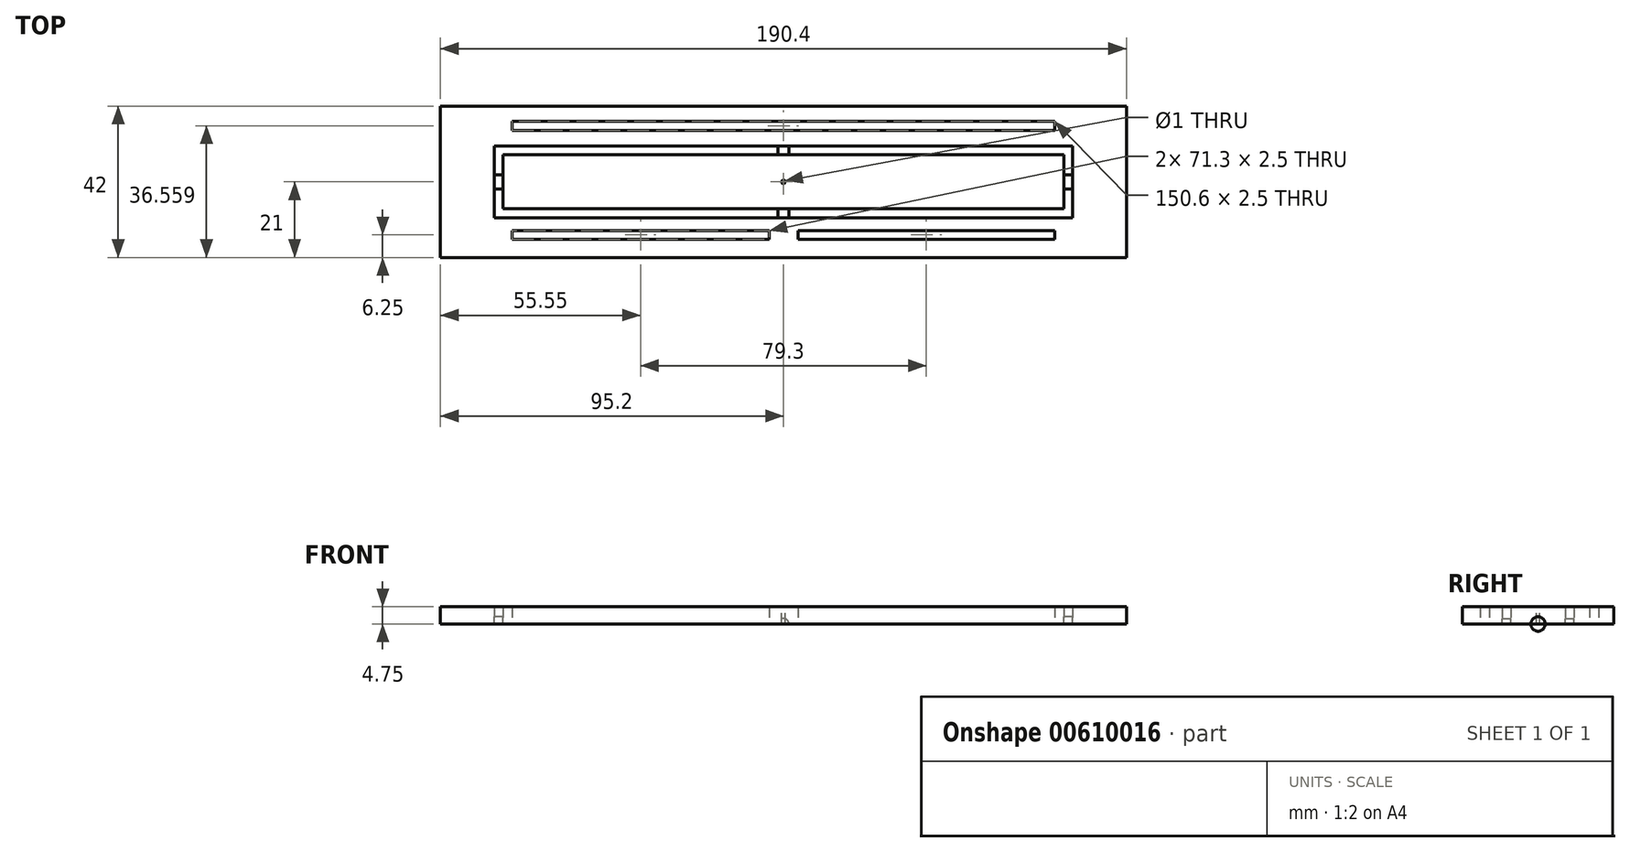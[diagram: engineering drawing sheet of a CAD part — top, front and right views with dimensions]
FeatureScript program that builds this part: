
annotation { "Feature Type Name" : "Feature", "Feature Type Description" : "" }
export const myFeature = defineFeature(function(context is Context, id is Id, definition is map)
    precondition{}
    {
        {
            var Q0;
            Q0=qCreatedBy(makeId("Front.planeOp"),FACE);
            var sketch = newSketch(context, id + "F0", { "sketchPlane" : qUnion([Q0])});
            skPoint(sketch, "E0.middle", {"position": v(0.08, 0) * mm});
            skLineSegment(sketch, "E1", {"start": v(-79.3, 0) * mm, "end": v(79.3, 0) * mm});
            skLineSegment(sketch, "E2.bottom", {"start": v(-79.3, 0) * mm, "end": v(-95.2, 0) * mm});
            skLineSegment(sketch, "E2.right", {"start": v(-95.2, 0) * mm, "end": v(-95.2, 4.75) * mm});
            skLineSegment(sketch, "E3", {"start": v(-79.3, 1) * mm, "end": v(-95.2, 4.75) * mm});
            skLineSegment(sketch, "E4.bottom", {"start": v(79.3, 0) * mm, "end": v(95.2, 0) * mm});
            skArc(sketch, "E5", {"start": v(1.5, 0) * mm, "mid": v(0, 1.5) * mm, "end": v(-1.5, 0) * mm});
            skLineSegment(sketch, "E6", {"start": v(-1.5, 0) * mm, "end": v(1.5, 0) * mm});
            skLineSegment(sketch, "E7", {"start": v(0, 0) * mm, "end": v(0, 4.75) * mm});
            skLineSegment(sketch, "E8", {"start": v(-95.2, 4.75) * mm, "end": v(95.2, 4.75) * mm});
            skLineSegment(sketch, "E9", {"start": v(95.2, 4.75) * mm, "end": v(95.2, 0) * mm});
            skLineSegment(sketch, "E10", {"start": v(79.3, 1) * mm, "end": v(95.2, 4.75) * mm});
            skArc(sketch, "E11", {"start": v(79.3, 1) * mm, "mid": v(0, 4.75) * mm, "end": v(-79.3, 1) * mm});
            skSolve(sketch);
        }
        {
            var Q0;
            Q0=qCreatedBy(makeId("Top.planeOp"),FACE);
            var sketch = newSketch(context, id + "F1", { "sketchPlane" : qUnion([Q0])});
            skPoint(sketch, "E12.middle", {"position": v(0, 0) * mm});
            skLineSegment(sketch, "E13.right", {"start": v(75.3, 16.8) * mm, "end": v(75.3, 14.3) * mm});
            skLineSegment(sketch, "E14.right", {"start": v(75.3, -13.5) * mm, "end": v(75.3, -16) * mm});
            skLineSegment(sketch, "E15.right", {"start": v(4, -13.5) * mm, "end": v(4, -16) * mm});
            skLineSegment(sketch, "E16.right", {"start": v(-4, -13.5) * mm, "end": v(-4, -16) * mm});
            skLineSegment(sketch, "E17.right", {"start": v(-75.3, -13.5) * mm, "end": v(-75.3, -16) * mm});
            skLineSegment(sketch, "E18.right", {"start": v(-75.3, 16.8) * mm, "end": v(-75.3, 14.3) * mm});
            skLineSegment(sketch, "E19", {"start": v(4, -13.5) * mm, "end": v(75.3, -13.5) * mm});
            skLineSegment(sketch, "E20", {"start": v(75.3, -16) * mm, "end": v(4, -16) * mm});
            skLineSegment(sketch, "E21", {"start": v(-75.3, -16) * mm, "end": v(-4, -16) * mm});
            skLineSegment(sketch, "E22", {"start": v(-4, -13.5) * mm, "end": v(-75.3, -13.5) * mm});
            skLineSegment(sketch, "E23", {"start": v(-75.3, 14.3) * mm, "end": v(75.3, 14.3) * mm});
            skLineSegment(sketch, "E24", {"start": v(75.3, 16.8) * mm, "end": v(-75.3, 16.8) * mm});
            skLineSegment(sketch, "E25.bottom", {"start": v(-80.3, 10) * mm, "end": v(80.3, 10) * mm});
            skLineSegment(sketch, "E25.top", {"start": v(-80.3, -10) * mm, "end": v(80.3, -10) * mm});
            skLineSegment(sketch, "E25.left", {"start": v(-80.3, 10) * mm, "end": v(-80.3, -10) * mm});
            skLineSegment(sketch, "E25.right", {"start": v(80.3, 10) * mm, "end": v(80.3, -10) * mm});
            skLineSegment(sketch, "E26.0", {"start": v(-77.8, 7.5) * mm, "end": v(77.8, 7.5) * mm});
            skLineSegment(sketch, "E26.1", {"start": v(-77.8, 7.5) * mm, "end": v(-77.8, -7.5) * mm});
            skLineSegment(sketch, "E26.2", {"start": v(-77.8, -7.5) * mm, "end": v(77.8, -7.5) * mm});
            skLineSegment(sketch, "E26.3", {"start": v(77.8, 7.5) * mm, "end": v(77.8, -7.5) * mm});
            skLineSegment(sketch, "E27", {"start": v(0, 14.3) * mm, "end": v(0, 10) * mm});
            skSolve(sketch);
        }
        {
            var Q0;
            {var subQ1=sQuery(id+"F0.wireOp",EDGE,"E3");Q0=makeQuery(id+"F0.imprint","IMPRINT",FACE,{"disambiguationData":[TD([[makeQuery(id+"F0.imprint","IMPRINT",EDGE,{"derivedFrom":subQ1}),1.0]])]});}
            var Q1;
            Q1=makeQuery(id+"F0.imprint","IMPRINT",FACE,{"disambiguationData":[TD([[makeQuery(id+"F0.imprint","IMPRINT",EDGE,{"derivedFrom":sQuery(id+"F0.wireOp",EDGE,"2Xmcz634-q65L-OcEz-RFky-VBpyImEll2yt.bottom")}),-1.0]])]});
            var Q2;
            Q2=makeQuery(id+"F0.imprint","IMPRINT",FACE,{"disambiguationData":[TD([[makeQuery(id+"F0.imprint","IMPRINT",EDGE,{"derivedFrom":sQuery(id+"F0.wireOp",EDGE,"E5")}),1.0]])]});
            var Q3;
            {var subQ7=sQuery(id+"F0.wireOp",EDGE,"CYJWQcW4-jkQO-EFny-5skn-M0ueQvAqL0zQ");Q3=makeQuery(id+"F0.imprint","IMPRINT",FACE,{"disambiguationData":[TD([[makeQuery(id+"F0.imprint","IMPRINT",EDGE,{"derivedFrom":subQ7}),-1.0]])]});}
            var Q4;
            {var subQ0=sQuery(id+"F0.wireOp",EDGE,"E3");Q4=makeQuery(id+"F0.imprint","IMPRINT",FACE,{"disambiguationData":[TD([[makeQuery(id+"F0.imprint","IMPRINT",EDGE,{"derivedFrom":subQ0}),-1.0]])]});}
            var Q5;
            {var subQ0=sQuery(id+"F0.wireOp",EDGE,"CYJWQcW4-jkQO-EFny-5skn-M0ueQvAqL0zQ");Q5=makeQuery(id+"F0.imprint","IMPRINT",FACE,{"disambiguationData":[TD([[makeQuery(id+"F0.imprint","IMPRINT",EDGE,{"derivedFrom":subQ0}),1.0]])]});}
            var Q6;
            {var subQ0=sQuery(id+"F0.wireOp",EDGE,"E4.bottom");Q6=makeQuery(id+"F0.imprint","IMPRINT",FACE,{"disambiguationData":[TD([[makeQuery(id+"F0.imprint","IMPRINT",EDGE,{"derivedFrom":subQ0}),1.0]])]});}
            var Q7;
            {var subQ3=sQuery(id+"F0.wireOp",EDGE,"E10");Q7=makeQuery(id+"F0.imprint","IMPRINT",FACE,{"disambiguationData":[TD([[makeQuery(id+"F0.imprint","IMPRINT",EDGE,{"derivedFrom":subQ3}),1.0]])]});}
            extrude(context, id + "F2", {"entities" : qUnion([Q0, Q1, Q2, Q3, Q4, Q5, Q6, Q7]), "depth" : 21 * mm, "offsetDistance" : 25 * mm, "hasSecondDirection" : true, "secondDirectionOppositeDirection" : true, "secondDirectionDepth" : 21 * mm});
        }
        {
            var Q0;
            Q0=qSketchRegion(id+"F1",true);
            extrude(context, id + "F3", {"entities" : qUnion([Q0]), "operationType" : NewBodyOperationType.REMOVE, "endBound" : BoundingType.UP_TO_NEXT, "depth" : 5 * mm, "offsetDistance" : 25 * mm});
        }
        {
            var Q0;
            Q0=makeQuery(id+"F3.boolean.opBoolean","SPLIT",FACE,{"disambiguationData":[TD([makeQuery(id+"F3.opExtrude","SWEPT_FACE",FACE,{"disambiguationData":[OSD([sQuery(id+"F1.wireOp",EDGE,"E26.0")])]})])],"derivedFrom":makeQuery(id+"F2.opExtrude","SWEPT_FACE",FACE,{"disambiguationData":[OSD([sQuery(id+"F0.wireOp",EDGE,"E8")])]})});
            var sketch = newSketch(context, id + "F4", { "sketchPlane" : qUnion([Q0])});
            skCircle(sketch, "E28", {"center": v(0, 0) * mm, "radius": 0.5 * mm});
            skSolve(sketch);
        }
        {
            var Q0;
            {var subQ4=sQuery(id+"F0.wireOp",EDGE,"E2.right");var subQ5=sQuery(id+"F0.wireOp",EDGE,"E1dovW2E-v4zk-sWPI-QtKG-T9o5jAE7GfwR.top");Q0=makeQuery(id+"F3.boolean.opBoolean","SPLIT",FACE,{"disambiguationData":[TD([makeQuery(id+"F2.opExtrude","SWEPT_FACE",FACE,{"disambiguationData":[OSD([subQ4])]})])],"derivedFrom":makeQuery(id+"F2.opExtrude","SWEPT_FACE",FACE,{"disambiguationData":[OSD([subQ5])]})});}
            var sketch = newSketch(context, id + "F5", { "sketchPlane" : qUnion([Q0])});
            skLineSegment(sketch, "E29.bottom", {"start": v(-80.3, 10) * mm, "end": v(-82.3, 10) * mm});
            skLineSegment(sketch, "E29.top", {"start": v(-80.3, -10) * mm, "end": v(-82.3, -10) * mm});
            skLineSegment(sketch, "E29.left", {"start": v(-80.3, 10) * mm, "end": v(-80.3, -10) * mm});
            skLineSegment(sketch, "E29.right", {"start": v(-82.3, 10) * mm, "end": v(-82.3, -10) * mm});
            skLineSegment(sketch, "E30.bottom", {"start": v(80.3, 10) * mm, "end": v(82.3, 10) * mm});
            skLineSegment(sketch, "E30.top", {"start": v(80.3, -10) * mm, "end": v(82.3, -10) * mm});
            skLineSegment(sketch, "E30.left", {"start": v(80.3, 10) * mm, "end": v(80.3, -10) * mm});
            skLineSegment(sketch, "E30.right", {"start": v(82.3, 10) * mm, "end": v(82.3, -10) * mm});
            skSolve(sketch);
        }
        {
            var Q0;
            Q0=makeQuery(id+"F2.opExtrude","SWEPT_FACE",FACE,{"disambiguationData":[OSD([sQuery(id+"F0.wireOp",EDGE,"E2.right")])]});
            var sketch = newSketch(context, id + "F6", { "sketchPlane" : qUnion([Q0])});
            skArc(sketch, "E31", {"start": v(2, 0) * mm, "mid": v(0, 2) * mm, "end": v(-2, 0) * mm});
            skLineSegment(sketch, "E32", {"start": v(-2, 0) * mm, "end": v(2, 0) * mm});
            skSolve(sketch);
        }
        {
            var Q0;
            Q0=qSketchRegion(id+"F6",true);
            extrude(context, id + "F7", {"entities" : qUnion([Q0]), "depth" : 0 * mm, "offsetDistance" : 25 * mm, "hasSecondDirection" : true, "secondDirectionOppositeDirection" : true, "secondDirectionDepth" : 190 * mm});
        }
        {
            var Q0;
            Q0=makeQuery(id+"F0.imprint","IMPRINT",FACE,{"disambiguationData":[TD([[makeQuery(id+"F0.imprint","IMPRINT",EDGE,{"derivedFrom":sQuery(id+"F0.wireOp",EDGE,"E5")}),1.0]])]});
            extrude(context, id + "F8", {"entities" : qUnion([Q0]), "operationType" : NewBodyOperationType.ADD, "depth" : 12 * mm, "offsetDistance" : 25 * mm, "hasSecondDirection" : true, "secondDirectionOppositeDirection" : true, "secondDirectionDepth" : 12 * mm});
        }
        {
            var Q0;
            Q0=makeQuery(id+"F1.imprint","IMPRINT",FACE,{"disambiguationData":[TD([[makeQuery(id+"F1.imprint","IMPRINT",EDGE,{"derivedFrom":sQuery(id+"F1.wireOp",EDGE,"E26.0")}),-1.0]])]});
            extrude(context, id + "F9", {"entities" : qUnion([Q0]), "operationType" : NewBodyOperationType.ADD, "depth" : 4.75 * mm, "offsetDistance" : 25 * mm});
        }
        {
            var Q0;
            Q0=makeQuery(id+"F4.imprint","IMPRINT",FACE,{"disambiguationData":[TD([[makeQuery(id+"F4.imprint","IMPRINT",EDGE,{"derivedFrom":sQuery(id+"F4.wireOp",EDGE,"E28")}),1.0]])]});
            extrude(context, id + "F10", {"entities" : qUnion([Q0]), "operationType" : NewBodyOperationType.REMOVE, "oppositeDirection" : true, "depth" : 5 * mm, "offsetDistance" : 25 * mm});
        }
    });
